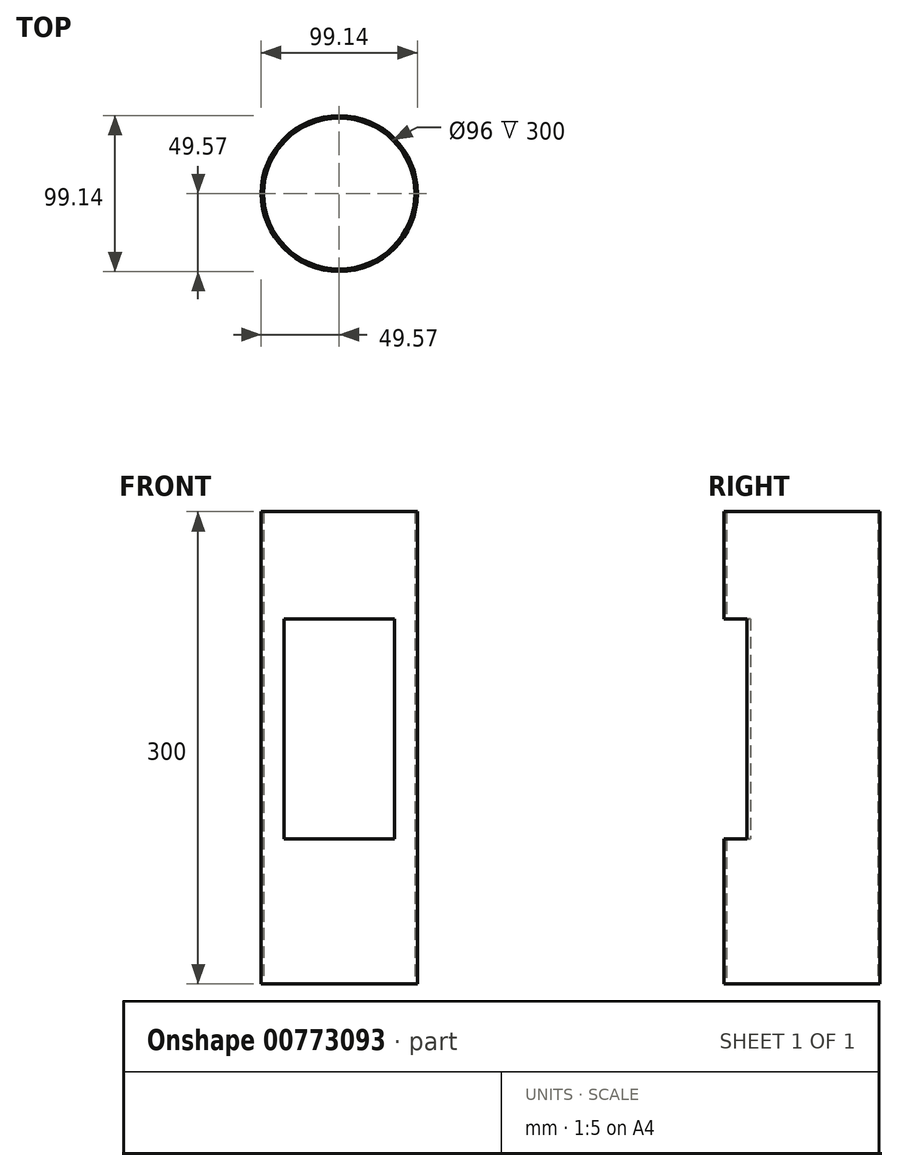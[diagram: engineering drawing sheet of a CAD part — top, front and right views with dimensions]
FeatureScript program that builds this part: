
annotation { "Feature Type Name" : "Feature", "Feature Type Description" : "" }
export const myFeature = defineFeature(function(context is Context, id is Id, definition is map)
    precondition{}
    {
        {
            var Q0;
            Q0=qCreatedBy(makeId("Top.planeOp"),FACE);
            var sketch = newSketch(context, id + "F0", { "sketchPlane" : qUnion([Q0])});
            skCircle(sketch, "E0", {"center": v(0, 0) * mm, "radius": 48 * mm});
            skCircle(sketch, "E1", {"center": v(0, 0) * mm, "radius": 49.57 * mm});
            skSolve(sketch);
        }
        {
            var Q0;
            Q0 = qSketchRegion(id + "F0", true);
            extrude(context, id + "F1", {"entities" : qUnion([Q0]), "depth" : 300 * mm, "offsetDistance" : 25 * mm});
        }
        {
            var Q0;
            Q0=qCreatedBy(makeId("Front.planeOp"),FACE);
            var sketch = newSketch(context, id + "F2", { "sketchPlane" : qUnion([Q0])});
            skLineSegment(sketch, "E2.bottom", {"start": v(-35, 232) * mm, "end": v(35, 232) * mm});
            skLineSegment(sketch, "E2.top", {"start": v(-35, 92) * mm, "end": v(35, 92) * mm});
            skLineSegment(sketch, "E2.left", {"start": v(-35, 232) * mm, "end": v(-35, 92) * mm});
            skLineSegment(sketch, "E2.right", {"start": v(35, 232) * mm, "end": v(35, 92) * mm});
            skSolve(sketch);
        }
        {
            var Q0;
            Q0 = qSketchRegion(id + "F2", true);
            extrude(context, id + "F3", {"entities" : qUnion([Q0]), "operationType" : NewBodyOperationType.REMOVE, "depth" : 100 * mm, "offsetDistance" : 25 * mm});
        }
    });
